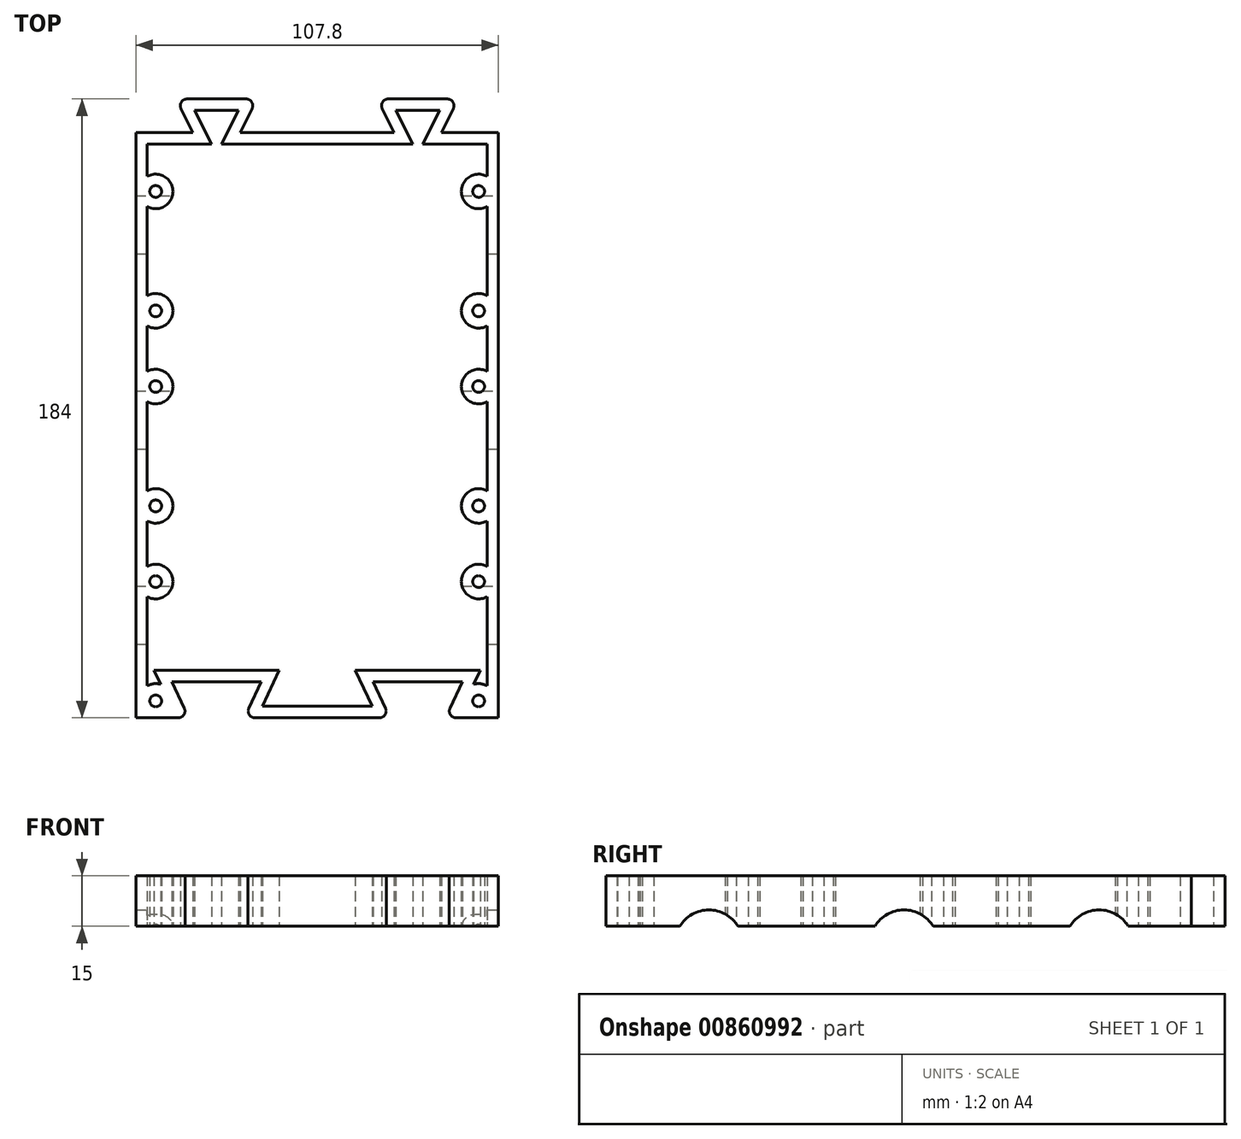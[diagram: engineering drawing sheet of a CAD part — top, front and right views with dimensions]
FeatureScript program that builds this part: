
annotation { "Feature Type Name" : "Feature", "Feature Type Description" : "" }
export const myFeature = defineFeature(function(context is Context, id is Id, definition is map)
    precondition{}
    {
        {
            var Q0;
            Q0=qCreatedBy(makeId("Top.planeOp"),FACE);
            var sketch = newSketch(context, id + "F0", { "sketchPlane" : qUnion([Q0])});
            skPoint(sketch, "E0", {"position": v(0, -174) * mm});
            skPoint(sketch, "E1", {"position": v(107.8, 0) * mm});
            skPoint(sketch, "E2", {"position": v(107.8, -174) * mm});
            skLineSegment(sketch, "E3", {"start": v(0, 0) * mm, "end": v(0, -174) * mm});
            skLineSegment(sketch, "E4", {"start": v(107.8, 0) * mm, "end": v(107.8, -174) * mm});
            skPoint(sketch, "E5", {"position": v(24, 0) * mm});
            skPoint(sketch, "E6", {"position": v(83.8, 0) * mm});
            skPoint(sketch, "E7", {"position": v(83.8, 10) * mm});
            skPoint(sketch, "E8", {"position": v(24, 10) * mm});
            skPoint(sketch, "E9", {"position": v(12, 10) * mm});
            skPoint(sketch, "E10", {"position": v(36, 10) * mm});
            skPoint(sketch, "E11", {"position": v(71.8, 10) * mm});
            skPoint(sketch, "E12", {"position": v(95.8, 10) * mm});
            skPoint(sketch, "E13", {"position": v(17, 0) * mm});
            skPoint(sketch, "E14", {"position": v(31, 0) * mm});
            skPoint(sketch, "E15", {"position": v(76.8, 0) * mm});
            skPoint(sketch, "E16", {"position": v(90.8, 0) * mm});
            skLineSegment(sketch, "E17", {"start": v(0, 0) * mm, "end": v(17, 0) * mm});
            skLineSegment(sketch, "E18", {"start": v(17, 0) * mm, "end": v(12, 10) * mm});
            skLineSegment(sketch, "E19", {"start": v(12, 10) * mm, "end": v(36, 10) * mm});
            skLineSegment(sketch, "E20", {"start": v(36, 10) * mm, "end": v(31, 0) * mm});
            skLineSegment(sketch, "E21", {"start": v(31, 0) * mm, "end": v(76.8, 0) * mm});
            skLineSegment(sketch, "E22", {"start": v(76.8, 0) * mm, "end": v(71.8, 10) * mm});
            skLineSegment(sketch, "E23", {"start": v(71.8, 10) * mm, "end": v(95.8, 10) * mm});
            skLineSegment(sketch, "E24", {"start": v(95.8, 10) * mm, "end": v(90.8, 0) * mm});
            skLineSegment(sketch, "E25", {"start": v(90.8, 0) * mm, "end": v(107.8, 0) * mm});
            skPoint(sketch, "E26", {"position": v(83.8, -174) * mm});
            skPoint(sketch, "E27", {"position": v(24, -174) * mm});
            skPoint(sketch, "E28", {"position": v(24, -163.25) * mm});
            skPoint(sketch, "E29", {"position": v(83.8, -163.25) * mm});
            skPoint(sketch, "E30", {"position": v(10.75, -163.25) * mm});
            skPoint(sketch, "E31", {"position": v(37.25, -163.25) * mm});
            skPoint(sketch, "E32", {"position": v(97.05, -163.25) * mm});
            skPoint(sketch, "E33", {"position": v(70.55, -163.25) * mm});
            skPoint(sketch, "E34", {"position": v(75.55, -174) * mm});
            skPoint(sketch, "E35", {"position": v(92.05, -174) * mm});
            skPoint(sketch, "E36", {"position": v(32.25, -174) * mm});
            skPoint(sketch, "E37", {"position": v(15.75, -174) * mm});
            skLineSegment(sketch, "E38", {"start": v(0, -174) * mm, "end": v(15.75, -174) * mm});
            skLineSegment(sketch, "E39", {"start": v(15.75, -174) * mm, "end": v(10.75, -163.25) * mm});
            skLineSegment(sketch, "E40", {"start": v(10.75, -163.25) * mm, "end": v(37.25, -163.25) * mm});
            skLineSegment(sketch, "E41", {"start": v(37.25, -163.25) * mm, "end": v(32.25, -174) * mm});
            skLineSegment(sketch, "E42", {"start": v(32.25, -174) * mm, "end": v(75.55, -174) * mm});
            skLineSegment(sketch, "E43", {"start": v(75.55, -174) * mm, "end": v(70.55, -163.25) * mm});
            skLineSegment(sketch, "E44", {"start": v(70.55, -163.25) * mm, "end": v(97.05, -163.25) * mm});
            skLineSegment(sketch, "E45", {"start": v(97.05, -163.25) * mm, "end": v(92.05, -174) * mm});
            skLineSegment(sketch, "E46", {"start": v(92.05, -174) * mm, "end": v(107.8, -174) * mm});
            skPoint(sketch, "E47", {"position": v(5.9, -169) * mm});
            skPoint(sketch, "E48", {"position": v(5.9, -133.5) * mm});
            skPoint(sketch, "E49.endSnap0", {"position": v(99.93, -174) * mm});
            skCircle(sketch, "E50", {"center": v(5.9, -169) * mm, "radius": 1.75 * mm});
            skCircle(sketch, "E51", {"center": v(5.9, -133.5) * mm, "radius": 1.75 * mm});
            skCircle(sketch, "E52.0.1.0", {"center": v(5.9, -111) * mm, "radius": 1.75 * mm});
            skCircle(sketch, "E52.0.2.0", {"center": v(5.9, -53) * mm, "radius": 1.75 * mm});
            skCircle(sketch, "E52.1.0.0", {"center": v(101.9, -169) * mm, "radius": 1.75 * mm});
            skCircle(sketch, "E52.1.1.0", {"center": v(101.9, -111) * mm, "radius": 1.75 * mm});
            skCircle(sketch, "E52.1.2.0", {"center": v(101.9, -53) * mm, "radius": 1.75 * mm});
            skLineSegment(sketch, "E52.direction1", {"start": v(5.9, -169) * mm, "end": v(101.9, -169) * mm, "construction": true});
            skLineSegment(sketch, "E52.direction2", {"start": v(5.9, -169) * mm, "end": v(5.9, -111) * mm, "construction": true});
            skCircle(sketch, "E53.0.3.0", {"center": v(5.9, 48.5) * mm, "radius": 1.75 * mm});
            skCircle(sketch, "E53.1.3.0", {"center": v(101.9, 48.5) * mm, "radius": 1.75 * mm});
            skLineSegment(sketch, "E53.direction2", {"start": v(5.9, -133.5) * mm, "end": v(5.9, -75.5) * mm, "construction": true});
            skCircle(sketch, "E54.0.1.0", {"center": v(5.9, -75.5) * mm, "radius": 1.75 * mm});
            skPoint(sketch, "E54.0.1.1", {"position": v(5.9, -75.5) * mm});
            skCircle(sketch, "E54.0.2.0", {"center": v(5.9, -17.5) * mm, "radius": 1.75 * mm});
            skPoint(sketch, "E54.0.2.1", {"position": v(5.9, -17.5) * mm});
            skCircle(sketch, "E54.1.0.0", {"center": v(101.9, -133.5) * mm, "radius": 1.75 * mm});
            skPoint(sketch, "E54.1.0.1", {"position": v(101.9, -133.5) * mm});
            skCircle(sketch, "E54.1.1.0", {"center": v(101.9, -75.5) * mm, "radius": 1.75 * mm});
            skPoint(sketch, "E54.1.1.1", {"position": v(101.9, -75.5) * mm});
            skCircle(sketch, "E54.1.2.0", {"center": v(101.9, -17.5) * mm, "radius": 1.75 * mm});
            skPoint(sketch, "E54.1.2.1", {"position": v(101.9, -17.5) * mm});
            skLineSegment(sketch, "E54.direction1", {"start": v(5.9, -133.5) * mm, "end": v(101.9, -133.5) * mm, "construction": true});
            skSolve(sketch);
        }
        {
            var Q0;
            Q0=makeQuery(id+"F0.imprint","IMPRINT",FACE,{"disambiguationData":[TD([[makeQuery(id+"F0.imprint","IMPRINT",EDGE,{"derivedFrom":sQuery(id+"F0.wireOp",EDGE,"E3")}),1.0]])]});
            var Q1;
            {var subQ3=sQuery(id+"F0.wireOp",EDGE,"E18");Q1=makeQuery(id+"F0.imprint","IMPRINT",FACE,{"disambiguationData":[TD([[makeQuery(id+"F0.imprint","IMPRINT",EDGE,{"derivedFrom":subQ3}),-1.0]])]});}
            var Q2;
            {var subQ0=sQuery(id+"F0.wireOp",EDGE,"E4");Q2=makeQuery(id+"F0.imprint","IMPRINT",FACE,{"disambiguationData":[TD([[makeQuery(id+"F0.imprint","IMPRINT",EDGE,{"derivedFrom":subQ0}),-1.0]])]});}
            extrude(context, id + "F1", {"entities" : qUnion([Q0, Q1, Q2]), "depth" : 15 * mm, "offsetDistance" : 25 * mm});
        }
        {
            var Q0;
            Q0=makeQuery(id+"F1.opExtrude","CAP_FACE",FACE,{"disambiguationData":[OSD([sQuery(id+"F0.wireOp",EDGE,"E3"),sQuery(id+"F0.wireOp",EDGE,"E4"),sQuery(id+"F0.wireOp",EDGE,"E17"),sQuery(id+"F0.wireOp",EDGE,"E18"),sQuery(id+"F0.wireOp",EDGE,"E19"),sQuery(id+"F0.wireOp",EDGE,"E20"),sQuery(id+"F0.wireOp",EDGE,"E21"),sQuery(id+"F0.wireOp",EDGE,"E22"),sQuery(id+"F0.wireOp",EDGE,"E23"),sQuery(id+"F0.wireOp",EDGE,"E24"),sQuery(id+"F0.wireOp",EDGE,"E25"),sQuery(id+"F0.wireOp",EDGE,"E38"),sQuery(id+"F0.wireOp",EDGE,"E39"),sQuery(id+"F0.wireOp",EDGE,"E40"),sQuery(id+"F0.wireOp",EDGE,"E41"),sQuery(id+"F0.wireOp",EDGE,"E42"),sQuery(id+"F0.wireOp",EDGE,"E43"),sQuery(id+"F0.wireOp",EDGE,"E44"),sQuery(id+"F0.wireOp",EDGE,"E45"),sQuery(id+"F0.wireOp",EDGE,"E46"),sQuery(id+"F0.wireOp",EDGE,"E50"),sQuery(id+"F0.wireOp",EDGE,"E51"),sQuery(id+"F0.wireOp",EDGE,"f23a599c-0a4c-42d7-8352-668d931a5bbb.0.1.0"),sQuery(id+"F0.wireOp",EDGE,"f23a599c-0a4c-42d7-8352-668d931a5bbb.0.2.0"),sQuery(id+"F0.wireOp",EDGE,"f23a599c-0a4c-42d7-8352-668d931a5bbb.0.3.0"),sQuery(id+"F0.wireOp",EDGE,"f23a599c-0a4c-42d7-8352-668d931a5bbb.1.0.0"),sQuery(id+"F0.wireOp",EDGE,"f23a599c-0a4c-42d7-8352-668d931a5bbb.1.1.0"),sQuery(id+"F0.wireOp",EDGE,"f23a599c-0a4c-42d7-8352-668d931a5bbb.1.2.0"),sQuery(id+"F0.wireOp",EDGE,"f23a599c-0a4c-42d7-8352-668d931a5bbb.1.3.0"),sQuery(id+"F0.wireOp",EDGE,"8d7e1e17-68d3-4274-bf32-06b6ae57f314.0.1.0"),sQuery(id+"F0.wireOp",EDGE,"8d7e1e17-68d3-4274-bf32-06b6ae57f314.0.2.0"),sQuery(id+"F0.wireOp",EDGE,"8d7e1e17-68d3-4274-bf32-06b6ae57f314.0.3.0"),sQuery(id+"F0.wireOp",EDGE,"8d7e1e17-68d3-4274-bf32-06b6ae57f314.1.0.0"),sQuery(id+"F0.wireOp",EDGE,"8d7e1e17-68d3-4274-bf32-06b6ae57f314.1.1.0"),sQuery(id+"F0.wireOp",EDGE,"8d7e1e17-68d3-4274-bf32-06b6ae57f314.1.2.0"),sQuery(id+"F0.wireOp",EDGE,"8d7e1e17-68d3-4274-bf32-06b6ae57f314.1.3.0")])],"isStart":false});
            var Q1;
            Q1=makeQuery(id+"F1.opExtrude","CAP_FACE",FACE,{"disambiguationData":[OSD([sQuery(id+"F0.wireOp",EDGE,"E3"),sQuery(id+"F0.wireOp",EDGE,"E4"),sQuery(id+"F0.wireOp",EDGE,"E17"),sQuery(id+"F0.wireOp",EDGE,"E18"),sQuery(id+"F0.wireOp",EDGE,"E19"),sQuery(id+"F0.wireOp",EDGE,"E20"),sQuery(id+"F0.wireOp",EDGE,"E21"),sQuery(id+"F0.wireOp",EDGE,"E22"),sQuery(id+"F0.wireOp",EDGE,"E23"),sQuery(id+"F0.wireOp",EDGE,"E24"),sQuery(id+"F0.wireOp",EDGE,"E25"),sQuery(id+"F0.wireOp",EDGE,"E38"),sQuery(id+"F0.wireOp",EDGE,"E39"),sQuery(id+"F0.wireOp",EDGE,"E40"),sQuery(id+"F0.wireOp",EDGE,"E41"),sQuery(id+"F0.wireOp",EDGE,"E42"),sQuery(id+"F0.wireOp",EDGE,"E43"),sQuery(id+"F0.wireOp",EDGE,"E44"),sQuery(id+"F0.wireOp",EDGE,"E45"),sQuery(id+"F0.wireOp",EDGE,"E46"),sQuery(id+"F0.wireOp",EDGE,"E50"),sQuery(id+"F0.wireOp",EDGE,"E51"),sQuery(id+"F0.wireOp",EDGE,"f23a599c-0a4c-42d7-8352-668d931a5bbb.0.1.0"),sQuery(id+"F0.wireOp",EDGE,"f23a599c-0a4c-42d7-8352-668d931a5bbb.0.2.0"),sQuery(id+"F0.wireOp",EDGE,"f23a599c-0a4c-42d7-8352-668d931a5bbb.0.3.0"),sQuery(id+"F0.wireOp",EDGE,"f23a599c-0a4c-42d7-8352-668d931a5bbb.1.0.0"),sQuery(id+"F0.wireOp",EDGE,"f23a599c-0a4c-42d7-8352-668d931a5bbb.1.1.0"),sQuery(id+"F0.wireOp",EDGE,"f23a599c-0a4c-42d7-8352-668d931a5bbb.1.2.0"),sQuery(id+"F0.wireOp",EDGE,"f23a599c-0a4c-42d7-8352-668d931a5bbb.1.3.0"),sQuery(id+"F0.wireOp",EDGE,"8d7e1e17-68d3-4274-bf32-06b6ae57f314.0.1.0"),sQuery(id+"F0.wireOp",EDGE,"8d7e1e17-68d3-4274-bf32-06b6ae57f314.0.2.0"),sQuery(id+"F0.wireOp",EDGE,"8d7e1e17-68d3-4274-bf32-06b6ae57f314.0.3.0"),sQuery(id+"F0.wireOp",EDGE,"8d7e1e17-68d3-4274-bf32-06b6ae57f314.1.0.0"),sQuery(id+"F0.wireOp",EDGE,"8d7e1e17-68d3-4274-bf32-06b6ae57f314.1.1.0"),sQuery(id+"F0.wireOp",EDGE,"8d7e1e17-68d3-4274-bf32-06b6ae57f314.1.2.0"),sQuery(id+"F0.wireOp",EDGE,"8d7e1e17-68d3-4274-bf32-06b6ae57f314.1.3.0")])],"isStart":true});
            shell(context, id + "F2", {"entities" : qUnion([Q0, Q1]), "thickness" : 3.4 * mm});
        }
        {
            var Q0;
            Q0=makeQuery(id+"F1.opExtrude","SWEPT_EDGE",EDGE,{"disambiguationData":[OSD([sQuery(id+"F0.wireOp",EDGE,"E38"),sQuery(id+"F0.wireOp",EDGE,"E39")])]});
            var Q1;
            Q1=makeQuery(id+"F1.opExtrude","SWEPT_EDGE",EDGE,{"disambiguationData":[OSD([sQuery(id+"F0.wireOp",EDGE,"E41"),sQuery(id+"F0.wireOp",EDGE,"E42")])]});
            var Q2;
            Q2=makeQuery(id+"F1.opExtrude","SWEPT_EDGE",EDGE,{"disambiguationData":[OSD([sQuery(id+"F0.wireOp",EDGE,"E42"),sQuery(id+"F0.wireOp",EDGE,"E43")])]});
            var Q3;
            Q3=makeQuery(id+"F1.opExtrude","SWEPT_EDGE",EDGE,{"disambiguationData":[OSD([sQuery(id+"F0.wireOp",EDGE,"E45"),sQuery(id+"F0.wireOp",EDGE,"E46")])]});
            var Q4;
            Q4=makeQuery(id+"F1.opExtrude","SWEPT_EDGE",EDGE,{"disambiguationData":[OSD([sQuery(id+"F0.wireOp",EDGE,"E18"),sQuery(id+"F0.wireOp",EDGE,"E19")])]});
            var Q5;
            Q5=makeQuery(id+"F1.opExtrude","SWEPT_EDGE",EDGE,{"disambiguationData":[OSD([sQuery(id+"F0.wireOp",EDGE,"E19"),sQuery(id+"F0.wireOp",EDGE,"E20")])]});
            var Q6;
            Q6=makeQuery(id+"F1.opExtrude","SWEPT_EDGE",EDGE,{"disambiguationData":[OSD([sQuery(id+"F0.wireOp",EDGE,"E22"),sQuery(id+"F0.wireOp",EDGE,"E23")])]});
            var Q7;
            Q7=makeQuery(id+"F1.opExtrude","SWEPT_EDGE",EDGE,{"disambiguationData":[OSD([sQuery(id+"F0.wireOp",EDGE,"E23"),sQuery(id+"F0.wireOp",EDGE,"E24")])]});
            fillet(context, id + "F3", {"entities" : qUnion([Q0, Q1, Q2, Q3, Q4, Q5, Q6, Q7]), "radius" : 2 * mm, "tangentPropagation" : true, "allowEdgeOverflow" : false});
        }
        {
            var Q0;
            Q0=makeQuery(id+"F1.opExtrude","SWEPT_FACE",FACE,{"disambiguationData":[OSD([sQuery(id+"F0.wireOp",EDGE,"E4")])]});
            var sketch = newSketch(context, id + "F4", { "sketchPlane" : qUnion([Q0])});
            skArc(sketch, "E55", {"start": v(-134.8, 0) * mm, "mid": v(-143.45, 4.88) * mm, "end": v(-152.1, 0) * mm});
            skArc(sketch, "E56.1.0.0", {"start": v(-76.8, 0) * mm, "mid": v(-85.45, 4.88) * mm, "end": v(-94.1, 0) * mm});
            skArc(sketch, "E56.2.0.0", {"start": v(-18.8, 0) * mm, "mid": v(-27.45, 4.88) * mm, "end": v(-36.1, 0) * mm});
            skLineSegment(sketch, "E56.direction1", {"start": v(-152.1, 0) * mm, "end": v(-94.1, 0) * mm, "construction": true});
            skSolve(sketch);
        }
        {
            var Q0;
            {var subQ0=sQuery(id+"F4.wireOp",EDGE,"E55");Q0=makeQuery(id+"F4.imprint","IMPRINT",FACE,{"disambiguationData":[TD([[makeQuery(id+"F4.imprint","IMPRINT",EDGE,{"derivedFrom":subQ0}),1.0]])]});}
            var Q1;
            {var subQ0=sQuery(id+"F4.wireOp",EDGE,"E56.1.0.0");Q1=makeQuery(id+"F4.imprint","IMPRINT",FACE,{"disambiguationData":[TD([[makeQuery(id+"F4.imprint","IMPRINT",EDGE,{"derivedFrom":subQ0}),1.0]])]});}
            var Q2;
            {var subQ0=sQuery(id+"F4.wireOp",EDGE,"E56.2.0.0");Q2=makeQuery(id+"F4.imprint","IMPRINT",FACE,{"disambiguationData":[TD([[makeQuery(id+"F4.imprint","IMPRINT",EDGE,{"derivedFrom":subQ0}),1.0]])]});}
            extrude(context, id + "F5", {"entities" : qUnion([Q0, Q1, Q2]), "operationType" : NewBodyOperationType.REMOVE, "oppositeDirection" : true, "depth" : 200 * mm, "offsetDistance" : 25 * mm});
        }
    });
